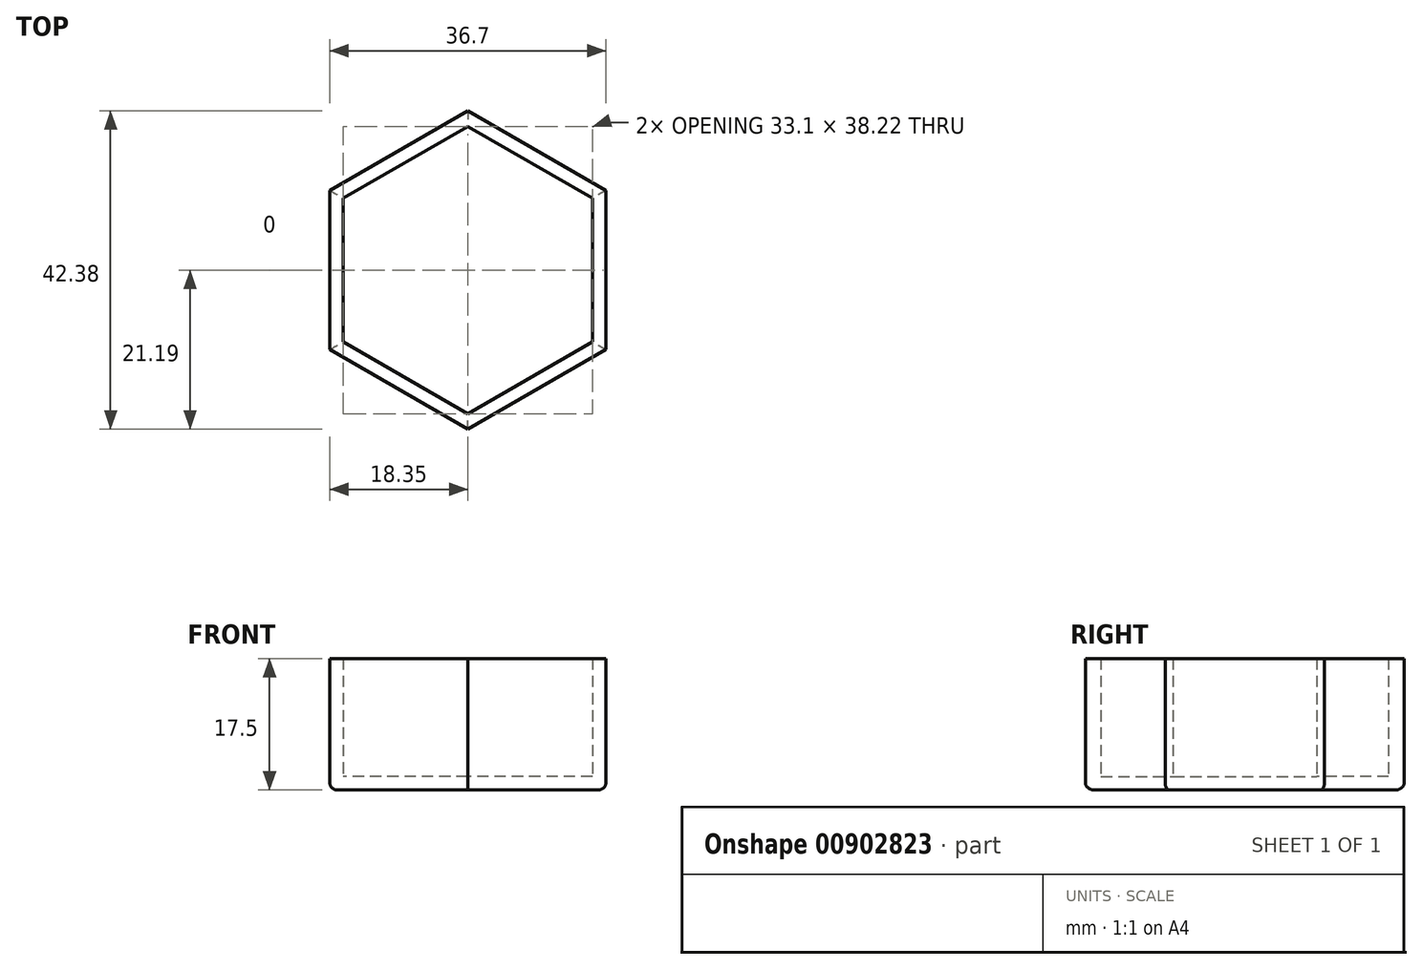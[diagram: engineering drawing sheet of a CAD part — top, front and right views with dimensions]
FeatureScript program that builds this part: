
annotation { "Feature Type Name" : "Feature", "Feature Type Description" : "" }
export const myFeature = defineFeature(function(context is Context, id is Id, definition is map)
    precondition{}
    {
        {
            var Q0;
            Q0=qCreatedBy(makeId("Top.planeOp"),FACE);
            var sketch = newSketch(context, id + "F0", { "sketchPlane" : qUnion([Q0])});
            skCircle(sketch, "E0.cCircle", {"center": v(0, 0) * mm, "radius": 18.35 * mm, "construction": true});
            skLineSegment(sketch, "E0.0", {"start": v(-18.35, -10.6) * mm, "end": v(-18.35, 10.6) * mm});
            skLineSegment(sketch, "E0.1", {"start": v(-18.35, 10.6) * mm, "end": v(0, 21.19) * mm});
            skLineSegment(sketch, "E0.2", {"start": v(0, 21.19) * mm, "end": v(18.35, 10.6) * mm});
            skLineSegment(sketch, "E0.3", {"start": v(18.35, 10.6) * mm, "end": v(18.35, -10.6) * mm});
            skLineSegment(sketch, "E0.4", {"start": v(18.35, -10.6) * mm, "end": v(0, -21.19) * mm});
            skLineSegment(sketch, "E0.5", {"start": v(0, -21.19) * mm, "end": v(-18.35, -10.6) * mm});
            skPoint(sketch, "E0.0.midPoint", {"position": v(-18.35, 0) * mm});
            skSolve(sketch);
        }
        {
            var Q0;
            Q0=makeQuery(id+"F0.imprint","IMPRINT",FACE,{"disambiguationData":[TD([[makeQuery(id+"F0.imprint","IMPRINT",EDGE,{"derivedFrom":sQuery(id+"F0.wireOp",EDGE,"E0.0")}),-1.0]])]});
            extrude(context, id + "F1", {"entities" : qUnion([Q0]), "depth" : 17.5 * mm, "offsetDistance" : 25 * mm});
        }
        {
            var Q0;
            Q0=makeQuery(id+"F1.opExtrude","CAP_FACE",FACE,{"disambiguationData":[OSD([sQuery(id+"F0.wireOp",EDGE,"E0.0"),sQuery(id+"F0.wireOp",EDGE,"E0.1"),sQuery(id+"F0.wireOp",EDGE,"E0.2"),sQuery(id+"F0.wireOp",EDGE,"E0.3"),sQuery(id+"F0.wireOp",EDGE,"E0.4"),sQuery(id+"F0.wireOp",EDGE,"E0.5")])],"isStart":false});
            shell(context, id + "F2", {"entities" : qUnion([Q0]), "thickness" : 1.8 * mm});
        }
        {
            var Q0;
            Q0=makeQuery(id+"F1.opExtrude","CAP_FACE",FACE,{"disambiguationData":[OSD([sQuery(id+"F0.wireOp",EDGE,"E0.0"),sQuery(id+"F0.wireOp",EDGE,"E0.1"),sQuery(id+"F0.wireOp",EDGE,"E0.2"),sQuery(id+"F0.wireOp",EDGE,"E0.3"),sQuery(id+"F0.wireOp",EDGE,"E0.4"),sQuery(id+"F0.wireOp",EDGE,"E0.5")])],"isStart":true});
            fillet(context, id + "F3", {"entities" : qUnion([Q0]), "radius" : 1 * mm, "tangentPropagation" : true, "allowEdgeOverflow" : false});
        }
    });
